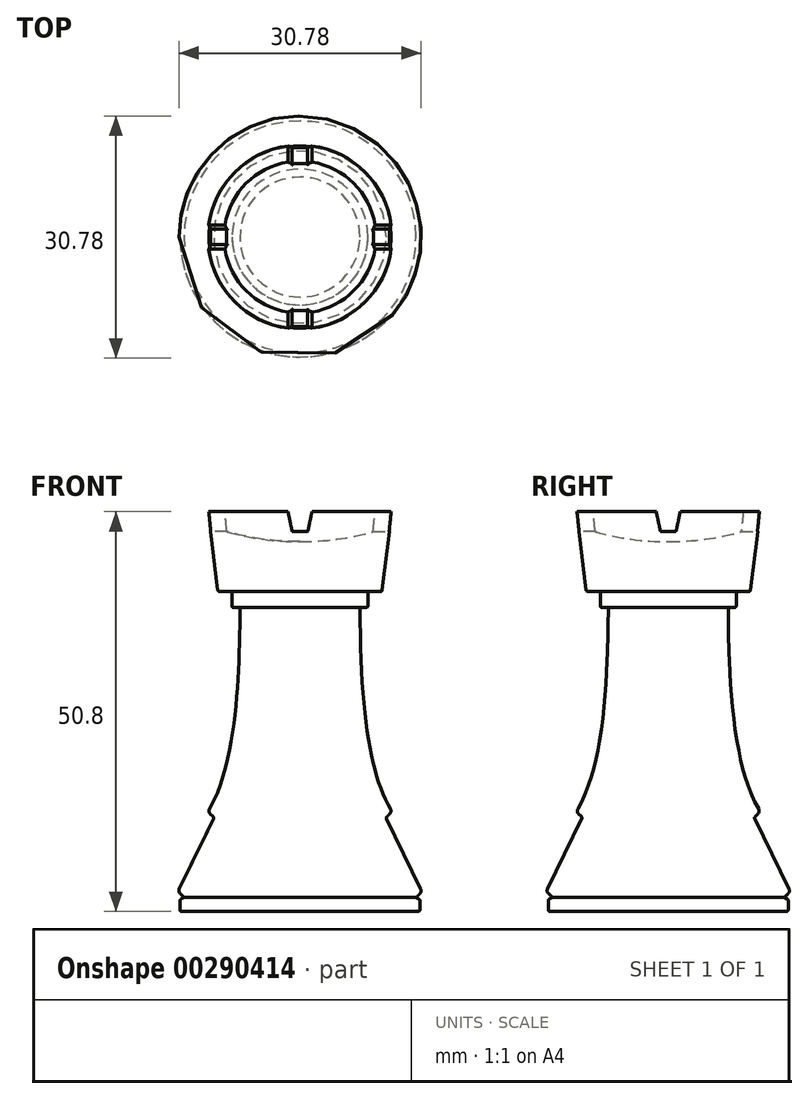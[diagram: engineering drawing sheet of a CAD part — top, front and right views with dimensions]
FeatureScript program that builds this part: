
annotation { "Feature Type Name" : "Feature", "Feature Type Description" : "" }
export const myFeature = defineFeature(function(context is Context, id is Id, definition is map)
    precondition{}
    {
        {
            var Q0;
            Q0=qCreatedBy(makeId("Front.planeOp"),FACE);
            var sketch = newSketch(context, id + "F0", { "sketchPlane" : qUnion([Q0])});
            skLineSegment(sketch, "E0", {"start": v(0, 0) * mm, "end": v(15.24, 0) * mm});
            skLineSegment(sketch, "E1", {"start": v(0, 50.8) * mm, "end": v(11.68, 50.8) * mm, "construction": true});
            skLineSegment(sketch, "E2", {"start": v(11.68, 50.8) * mm, "end": v(10.41, 40.64) * mm});
            skLineSegment(sketch, "E3", {"start": v(10.41, 40.64) * mm, "end": v(8.64, 40.64) * mm});
            skLineSegment(sketch, "E4", {"start": v(8.64, 40.64) * mm, "end": v(8.64, 38.6) * mm});
            skLineSegment(sketch, "E5", {"start": v(8.64, 38.6) * mm, "end": v(7.62, 38.6) * mm});
            skFitSpline(sketch, "E6", {"points": [v(7.62, 38.6) * mm, v(11.68, 12.7) * mm], "startDerivative": vector(0.12, -41.88) * mm, "endDerivative": vector(8.06, -13.3) * mm});
            skLineSegment(sketch, "E7", {"start": v(11.68, 12.7) * mm, "end": v(10.92, 11.94) * mm});
            skLineSegment(sketch, "E8", {"start": v(10.92, 11.94) * mm, "end": v(15.5, 2.54) * mm});
            skLineSegment(sketch, "E9", {"start": v(15.5, 2.54) * mm, "end": v(14.73, 1.78) * mm});
            skLineSegment(sketch, "E10", {"start": v(14.73, 1.78) * mm, "end": v(15.24, 1.52) * mm});
            skLineSegment(sketch, "E11", {"start": v(15.24, 1.52) * mm, "end": v(15.24, 0) * mm});
            skLineSegment(sketch, "E12", {"start": v(0, 50.8) * mm, "end": v(0, 0) * mm});
            skArc(sketch, "E13", {"start": v(0, 46.99) * mm, "mid": v(4.71, 47.3) * mm, "end": v(9.33, 48.26) * mm});
            skLineSegment(sketch, "E14", {"start": v(11.68, 50.8) * mm, "end": v(9.65, 50.8) * mm});
            skLineSegment(sketch, "E15", {"start": v(9.65, 50.8) * mm, "end": v(9.33, 48.26) * mm});
            skSolve(sketch);
        }
        {
            var Q0;
            Q0=makeQuery(id+"F0.imprint","IMPRINT",FACE,{"disambiguationData":[TD([[makeQuery(id+"F0.imprint","IMPRINT",EDGE,{"derivedFrom":sQuery(id+"F0.wireOp",EDGE,"E0")}),1.0]])]});
            var Q1;
            Q1=sQuery(id+"F0.wireOp",EDGE,"E12");
            revolve(context, id + "F1", {"entities" : qUnion([Q0]), "axis" : qUnion([Q1]), "revolveType" : RevolveType.FULL});
        }
        {
            var Q0;
            Q0=makeQuery(id+"F2tOPzGwXFgAwZ8_1.boolean.opBoolean","SPLIT",FACE,{"disambiguationData":[TD([makeQuery(id+"F2tOPzGwXFgAwZ8_1.opExtrude","SWEPT_FACE",FACE,{"disambiguationData":[OSD([sQuery(id+"FzdtRuaRfZORibA_1.wireOp",EDGE,"ww4pheE7-PuIm-I4Cx-NB4c-mAh5gk0yRajL")])]})])],"derivedFrom":makeQuery(id+"F1.opRevolve","SWEPT_FACE",FACE,{"disambiguationData":[OSD([sQuery(id+"F0.wireOp",EDGE,"E14")])]})});
            var sketch = newSketch(context, id + "F2", { "sketchPlane" : qUnion([Q0])});
            skLineSegment(sketch, "E16", {"start": v(-12.49, 1.52) * mm, "end": v(-7.54, 1.52) * mm});
            skLineSegment(sketch, "E17", {"start": v(-7.54, 1.52) * mm, "end": v(-7.54, -1.52) * mm});
            skLineSegment(sketch, "E18", {"start": v(-7.54, -1.52) * mm, "end": v(-12.49, -1.52) * mm});
            skLineSegment(sketch, "E19", {"start": v(-12.49, -1.52) * mm, "end": v(-12.49, 1.52) * mm});
            skSolve(sketch);
        }
        {
            var Q0;
            {var subQ0=sQuery(id+"F2.wireOp",EDGE,"E16");var subQ1=sQuery(id+"F0.wireOp",EDGE,"E2");var subQ2=sQuery(id+"F0.wireOp",EDGE,"E14");var subQ4=makeQuery(id+"F2tOPzGwXFgAwZ8_1.opExtrude","SWEPT_FACE",FACE,{"disambiguationData":[OSD([sQuery(id+"FzdtRuaRfZORibA_1.wireOp",EDGE,"ww4pheE7-PuIm-I4Cx-NB4c-mAh5gk0yRajL")])]});var subQ5=makeQuery(id+"F2tOPzGwXFgAwZ8_1.boolean.opBoolean","SPLIT",EDGE,{"disambiguationData":[TD([subQ4])],"derivedFrom":makeQuery(id+"F1.opRevolve","SWEPT_EDGE",EDGE,{"disambiguationData":[OSD([subQ1,subQ2])]})});var subQ6=makeQuery(id+"F2.imprint","INTERSECT",VERTEX,{"derivedFrom":[subQ5,subQ0]});Q0=makeQuery(id+"F2.imprint","IMPRINT",FACE,{"disambiguationData":[TD([[makeQuery(id+"F2.imprint","IMPRINT",EDGE,{"disambiguationData":[TD([[subQ6,-1.0]])],"derivedFrom":subQ0}),-1.0]])]});}
            var Q1;
            {var subQ0=sQuery(id+"F2.wireOp",EDGE,"E19");Q1=makeQuery(id+"F2.imprint","IMPRINT",FACE,{"disambiguationData":[TD([[makeQuery(id+"F2.imprint","IMPRINT",EDGE,{"derivedFrom":subQ0}),-1.0]])]});}
            var Q2;
            {var subQ0=sQuery(id+"F2.wireOp",EDGE,"E17");Q2=makeQuery(id+"F2.imprint","IMPRINT",FACE,{"disambiguationData":[TD([[makeQuery(id+"F2.imprint","IMPRINT",EDGE,{"derivedFrom":subQ0}),-1.0]])]});}
            extrude(context, id + "F3", {"entities" : qUnion([Q0, Q1, Q2]), "oppositeDirection" : true, "depth" : 2.54 * mm, "hasDraft" : true, "draftAngle" : 12 * degree, "draftPullDirection" : true});
        }
        {
            var Q0;
            Q0=makeQuery(id+"F3.opExtrude","SWEPT_BODY",BODY,{"disambiguationData":[OSD([sQuery(id+"F2.wireOp",EDGE,"E16"),sQuery(id+"F2.wireOp",EDGE,"E17"),sQuery(id+"F2.wireOp",EDGE,"E18"),sQuery(id+"F2.wireOp",EDGE,"E19")])]});
            var Q1;
            Q1=makeQuery(id+"F1.opRevolve","SWEPT_EDGE",EDGE,{"disambiguationData":[OSD([sQuery(id+"F0.wireOp",EDGE,"E2"),sQuery(id+"F0.wireOp",EDGE,"E14")])]});
            circularPattern(context, id + "F4", {"operationType" : NewBodyOperationType.REMOVE, "entities" : qUnion([Q0]), "axis" : qUnion([Q1]), "angle" : 360 * degree, "instanceCount" : 4, "equalSpace" : true});
        }
        {
            var Q0;
            Q0=makeQuery(id+"F1.opRevolve","SWEPT_EDGE",EDGE,{"disambiguationData":[OSD([sQuery(id+"F0.wireOp",EDGE,"E10"),sQuery(id+"F0.wireOp",EDGE,"E11")])]});
            var Q1;
            Q1=makeQuery(id+"F1.opRevolve","SWEPT_EDGE",EDGE,{"disambiguationData":[OSD([sQuery(id+"F0.wireOp",EDGE,"E7"),sQuery(id+"F0.wireOp",EDGE,"E8")])]});
            var Q2;
            Q2=makeQuery(id+"F1.opRevolve","SWEPT_EDGE",EDGE,{"disambiguationData":[OSD([sQuery(id+"F0.wireOp",EDGE,"E0"),sQuery(id+"F0.wireOp",EDGE,"E11")])]});
            var Q3;
            Q3=makeQuery(id+"F1.opRevolve","SWEPT_EDGE",EDGE,{"disambiguationData":[OSD([sQuery(id+"F0.wireOp",EDGE,"E4"),sQuery(id+"F0.wireOp",EDGE,"E5")])]});
            var Q4;
            Q4=makeQuery(id+"F1.opRevolve","SWEPT_EDGE",EDGE,{"disambiguationData":[OSD([sQuery(id+"F0.wireOp",EDGE,"E2"),sQuery(id+"F0.wireOp",EDGE,"E3")])]});
            var Q5;
            {var subQ0=sQuery(id+"F2.wireOp",EDGE,"E18");var subQ3=sQuery(id+"F0.wireOp",EDGE,"E15");var subQ4=makeQuery(id+"F1.opRevolve","SWEPT_FACE",FACE,{"disambiguationData":[OSD([subQ3])]});var subQ5=sQuery(id+"F0.wireOp",EDGE,"E13");var subQ6=makeQuery(id+"F1.opRevolve","SWEPT_FACE",FACE,{"disambiguationData":[OSD([subQ5])]});Q5=makeQuery(id+"F4.boolean.opBoolean","SPLIT",EDGE,{"disambiguationData":[topologyDisambiguationEdgeConnected([subQ6,subQ4]),TD([makeQuery(id+"F4.opPattern","COPY",FACE,{"derivedFrom":makeQuery(id+"F3.opExtrude","SWEPT_FACE",FACE,{"disambiguationData":[OSD([subQ0])]}),"instanceName":"2"})])],"derivedFrom":makeQuery(id+"F1.opRevolve","SWEPT_EDGE",EDGE,{"disambiguationData":[OSD([subQ5,subQ3])]})});}
            var Q6;
            {var subQ0=sQuery(id+"F2.wireOp",EDGE,"E18");var subQ3=sQuery(id+"F0.wireOp",EDGE,"E15");var subQ4=makeQuery(id+"F1.opRevolve","SWEPT_FACE",FACE,{"disambiguationData":[OSD([subQ3])]});var subQ5=sQuery(id+"F0.wireOp",EDGE,"E13");var subQ6=makeQuery(id+"F1.opRevolve","SWEPT_FACE",FACE,{"disambiguationData":[OSD([subQ5])]});Q6=makeQuery(id+"F4.boolean.opBoolean","SPLIT",EDGE,{"disambiguationData":[topologyDisambiguationEdgeConnected([subQ6,subQ4]),TD([makeQuery(id+"F3.opExtrude","SWEPT_FACE",FACE,{"disambiguationData":[OSD([subQ0])]})])],"derivedFrom":makeQuery(id+"F1.opRevolve","SWEPT_EDGE",EDGE,{"disambiguationData":[OSD([subQ5,subQ3])]})});}
            var Q7;
            {var subQ0=sQuery(id+"F2.wireOp",EDGE,"E18");var subQ3=sQuery(id+"F0.wireOp",EDGE,"E15");var subQ4=makeQuery(id+"F1.opRevolve","SWEPT_FACE",FACE,{"disambiguationData":[OSD([subQ3])]});var subQ5=sQuery(id+"F0.wireOp",EDGE,"E13");var subQ6=makeQuery(id+"F1.opRevolve","SWEPT_FACE",FACE,{"disambiguationData":[OSD([subQ5])]});Q7=makeQuery(id+"F4.boolean.opBoolean","SPLIT",EDGE,{"disambiguationData":[topologyDisambiguationEdgeConnected([subQ6,subQ4]),TD([makeQuery(id+"F4.opPattern","COPY",FACE,{"derivedFrom":makeQuery(id+"F3.opExtrude","SWEPT_FACE",FACE,{"disambiguationData":[OSD([subQ0])]}),"instanceName":"1"})])],"derivedFrom":makeQuery(id+"F1.opRevolve","SWEPT_EDGE",EDGE,{"disambiguationData":[OSD([subQ5,subQ3])]})});}
            var Q8;
            {var subQ1=sQuery(id+"F2.wireOp",EDGE,"E16");var subQ3=sQuery(id+"F0.wireOp",EDGE,"E15");var subQ4=makeQuery(id+"F1.opRevolve","SWEPT_FACE",FACE,{"disambiguationData":[OSD([subQ3])]});var subQ5=sQuery(id+"F0.wireOp",EDGE,"E13");var subQ6=makeQuery(id+"F1.opRevolve","SWEPT_FACE",FACE,{"disambiguationData":[OSD([subQ5])]});Q8=makeQuery(id+"F4.boolean.opBoolean","SPLIT",EDGE,{"disambiguationData":[topologyDisambiguationEdgeConnected([subQ6,subQ4]),TD([makeQuery(id+"F3.opExtrude","SWEPT_FACE",FACE,{"disambiguationData":[OSD([subQ1])]})])],"derivedFrom":makeQuery(id+"F1.opRevolve","SWEPT_EDGE",EDGE,{"disambiguationData":[OSD([subQ5,subQ3])]})});}
            fillet(context, id + "F5", {"entities" : qUnion([Q0, Q1, Q2, Q3, Q4, Q5, Q6, Q7, Q8]), "radius" : 0.25 * mm, "tangentPropagation" : true, "allowEdgeOverflow" : false});
        }
        {
            var Q0;
            Q0=makeQuery(id+"F1.opRevolve","SWEPT_EDGE",EDGE,{"disambiguationData":[OSD([sQuery(id+"F0.wireOp",EDGE,"E6"),sQuery(id+"F0.wireOp",EDGE,"E7")])]});
            var Q1;
            Q1=makeQuery(id+"F1.opRevolve","SWEPT_EDGE",EDGE,{"disambiguationData":[OSD([sQuery(id+"F0.wireOp",EDGE,"E8"),sQuery(id+"F0.wireOp",EDGE,"E9")])]});
            fillet(context, id + "F6", {"entities" : qUnion([Q0, Q1]), "radius" : 0.5 * mm, "tangentPropagation" : true, "allowEdgeOverflow" : false});
        }
    });
